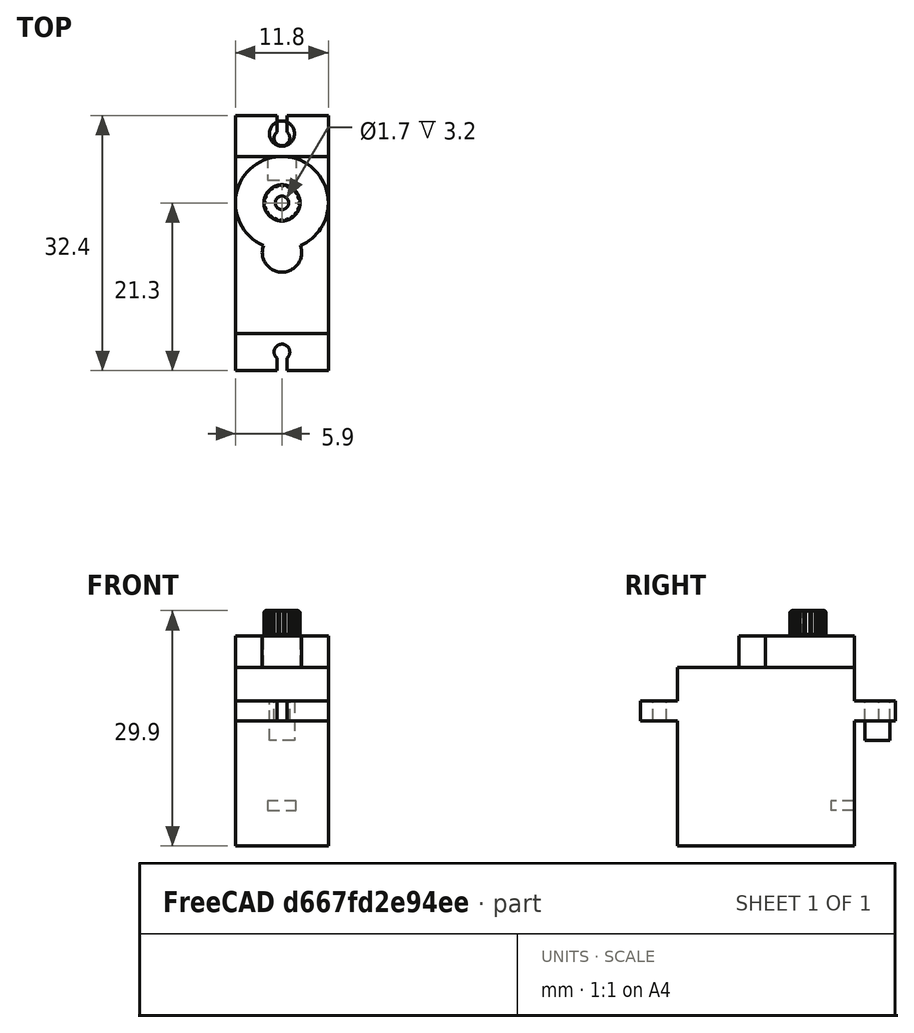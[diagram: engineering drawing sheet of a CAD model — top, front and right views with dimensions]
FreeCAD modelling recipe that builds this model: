
FCSTD DOCUMENT  (FreeCAD 0.16R6706 (Git))
Label: sg90
License: All rights reserved
LicenseURL: http://en.wikipedia.org/wiki/All_rights_reserved
objects: Sketcher::SketchObject×2, Part::Feature×1, PartDesign::Pocket×1
note: 5 computed .brp shape members not serialized (recipe doc carries the construction recipe); baked Part::Feature solids carry a one-line shape summary decoded from their .brp

FEATURE [Part::Feature] Part__Feature  label="Servo-sg90-final"
  shape: bbox 11.8 x 32.4 x 29.9 mm, 77 faces (baked)
FEATURE [Sketcher::SketchObject] Sketch
  Placement = pos=(0,0,18.4) rot=(0,0,1;0rad)
  Support = -> Part__Feature [Face12]
  sketch-geometry (1):
    g0: Circle CenterX=0 CenterY=25.4 CenterZ=0 NormalX=0 NormalY=0 NormalZ=1 Radius=1.6
  constraints (3):
    c: PointOnObject(g0,g-2)
    c: Radius(g0) = 1.6
    c: Distance(g-1,g0) = 25.4
FEATURE [Sketcher::SketchObject] Sketch001
  Placement = pos=(0,0,18.4) rot=(0,0,1;0rad)
  sketch-geometry (1):
    g0: Circle CenterX=0 CenterY=-2.9 CenterZ=0 NormalX=0 NormalY=0 NormalZ=1 Radius=1.6
  constraints (3):
    c: PointOnObject(g0,g-2)
    c: Radius(g0) = 1.6
    c: Distance(g-1,g0) = 2.9
FEATURE [PartDesign::Pocket] Pocket
  Length = 5
  Sketch = -> Sketch
  Type = 0
